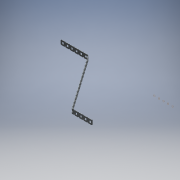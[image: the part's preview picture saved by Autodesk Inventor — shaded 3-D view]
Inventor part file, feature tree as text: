
AUTODESK INVENTOR PART (.ipt)
format: ipt  version: 2018 (Build 220112000, 112)  size: 659,456 bytes
history: native  units: mm (DEFAULTED — no unit token found)
features: other x26, extrude x25, sketch x4, sheet_metal_op x3, pattern_linear x2
ambient origin geometry x8: Origin, YZ Plane, XZ Plane, XY Plane, X Axis, Y Axis, Z Axis, Center Point
bodies: Solid1 (feature_tree)
feature tree (60):
  sheet_metal_op  "Face1"
  pattern_linear  "Rectangular Pattern1"  Spacing1=1.905mm  [1 undecoded]
  pattern_linear  "Rectangular Pattern2"  Spacing1=1.905mm  [1 undecoded]
  sheet_metal_op  "Fold1"
  sheet_metal_op  "Fold2"
  sketch  "Sketch1"  dims[d0=12.7mm]
  other  "Plate1"
  sketch  "Sketch4"  dims[d1=12.7mm]
  other  "Srf1"
  other  "Srf2"
  other  "Srf3"
  other  "Srf4"
  other  "Srf5"
  other  "Srf6"
  other  "Srf7"
  other  "Srf8"
  other  "Srf9"
  other  "Srf10"
  other  "Srf11"
  other  "Srf12"
  other  "Srf13"
  other  "Srf14"
  other  "Srf15"
  other  "Srf16"
  other  "Srf17"
  other  "Srf18"
  other  "Srf19"
  other  "Srf20"
  other  "Srf21"
  other  "Srf22"
  other  "Srf23"
  other  "Srf24"
  other  "Srf25"
  sketch  "Sketch5"  dims[d2=1.905mm]
  sketch  "Sketch6"  dims[d3=1.905mm d4=1.905mm d5=1.905mm d6=1.905mm d7=1.905mm d8=1.905mm d9=1.905mm d10=4.6228mm d11=4.6228mm d12=4.064mm d13=4.064mm d14=1.27mm d15=250.0mm d17=12.7mm d18=0.508mm d19=25.4mm d20=0.0mm d21=250.0mm d23=12.7mm d24=0.0mm d25=0.0mm d26=0.0mm d27=0.0mm d28=0.0mm d29=0.0mm d30=0.0mm d31=0.0mm d32=0.0mm d33=0.0mm d34=0.0mm d35=0.0mm d36=0.0mm d37=0.0mm d38=0.0mm d39=0.0mm d40=0.0mm d41=0.0mm d42=0.0mm d43=0.0mm d44=0.0mm d45=0.0mm d46=0.0mm d47=0.0mm d48=0.0mm d49=0.0mm d50=0.0mm d51=0.0mm d52=0.0mm d53=0.0mm d54=0.0mm d55=0.0mm d56=0.0mm d57=0.0mm d58=0.0mm d59=0.0mm d60=0.0mm d61=0.0mm d62=0.0mm d63=0.0mm d64=1.27mm d65=1.27mm d66=0.635mm d67=2.54mm d68=1.27mm d69=9.599311mm d70=1.27mm d71=1.27mm d72=0.635mm d73=2.54mm d74=1.27mm d75=9.599311mm d76=1.27mm]
  extrude  "ExtrusionSrf1"  Depth=1.27mm
  extrude  "ExtrusionSrf2"  Depth=1.27mm
  extrude  "ExtrusionSrf3"  Depth=1.27mm
  extrude  "ExtrusionSrf4"  Depth=1.27mm
  extrude  "ExtrusionSrf5"  Depth=4.6228mm
  extrude  "ExtrusionSrf6"  Depth=4.6228mm
  extrude  "ExtrusionSrf7"  Depth=4.064mm
  extrude  "ExtrusionSrf8"  Depth=4.064mm
  extrude  "ExtrusionSrf9"  Depth=1.27mm
  extrude  "ExtrusionSrf10"  Depth=12.7mm
  extrude  "ExtrusionSrf11"  Depth=0.508mm
  extrude  "ExtrusionSrf12"  Depth=1.27mm TaperAngle=0.0deg
  extrude  "ExtrusionSrf13"  Depth=12.7mm
  extrude  "ExtrusionSrf14"  Depth=1.27mm
  extrude  "ExtrusionSrf15"  Depth=1.27mm
  extrude  "ExtrusionSrf16"  Depth=1.27mm
  extrude  "ExtrusionSrf17"  Depth=2.54mm
  extrude  "ExtrusionSrf18"  Depth=1.27mm
  extrude  "ExtrusionSrf19"  Depth=1.27mm
  extrude  "ExtrusionSrf20"  Depth=1.27mm
  extrude  "ExtrusionSrf21"  Depth=1.27mm
  extrude  "ExtrusionSrf22"  Depth=2.54mm
  extrude  "ExtrusionSrf23"  Depth=1.27mm
  extrude  "ExtrusionSrf24"  Depth=1.27mm
  extrude  "ExtrusionSrf25"  [1 undecoded]
note: 3 required parameter values undecoded (feature->parameter linkage not recoverable at this tier; creation-order binding heuristic only, values carry confidence <= 0.55)
